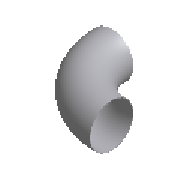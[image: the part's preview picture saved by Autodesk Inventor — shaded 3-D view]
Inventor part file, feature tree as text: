
AUTODESK INVENTOR PART (.ipt)
format: ipt  version: 2024.2 (Build 282272000, 272)  size: 180,224 bytes
history: native  units: mm (DEFAULTED — no unit token found)
features: other x4, sweep x1
ambient origin geometry x8: Origin, YZ Plane, XZ Plane, XY Plane, X Axis, Y Axis, Z Axis, Center Point
bodies: Solid1 (feature_tree)
feature tree (5):
  sweep  "Sweep1"
  other  "Work Point1"
  other  "Work Axis1"
  other  "Work Point2"
  other  "Work Axis2"
